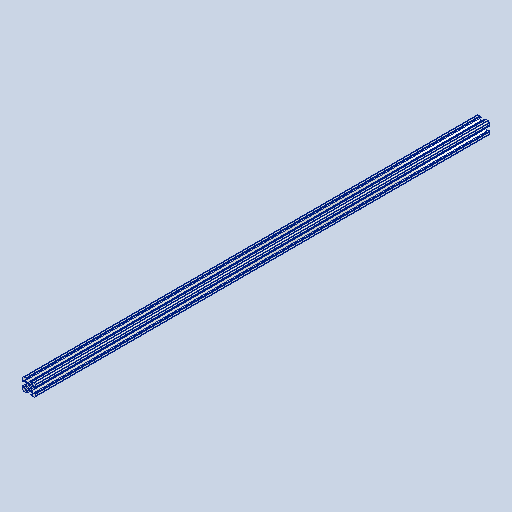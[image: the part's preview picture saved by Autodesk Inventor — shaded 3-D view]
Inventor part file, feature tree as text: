
AUTODESK INVENTOR PART (.ipt)
format: ipt  version: 2023 (Build 270158000, 158)  size: 492,032 bytes
history: native  units: in
note: dims shown in document units (in); Inventor stores cm internally (conversion verified against a paired STEP export)
features: extrude x1, sketch x1, projected_geometry x1, other x1
ambient origin geometry x8: Origin, YZ Plane, XZ Plane, XY Plane, X Axis, Y Axis, Z Axis, Center Point
bodies: Solid1 (feature_tree)
feature tree (4):
  extrude  "Extrusion1"  [1 undecoded]
  sketch  "Sketch1"  dims[d0=24.0in d1=0.0in]
  projected_geometry  "Projected Loop1"
  other  "Boss-Extrude1"
note: 1 required parameter value undecoded (feature->parameter linkage not recoverable at this tier; creation-order binding heuristic only, values carry confidence <= 0.55)
